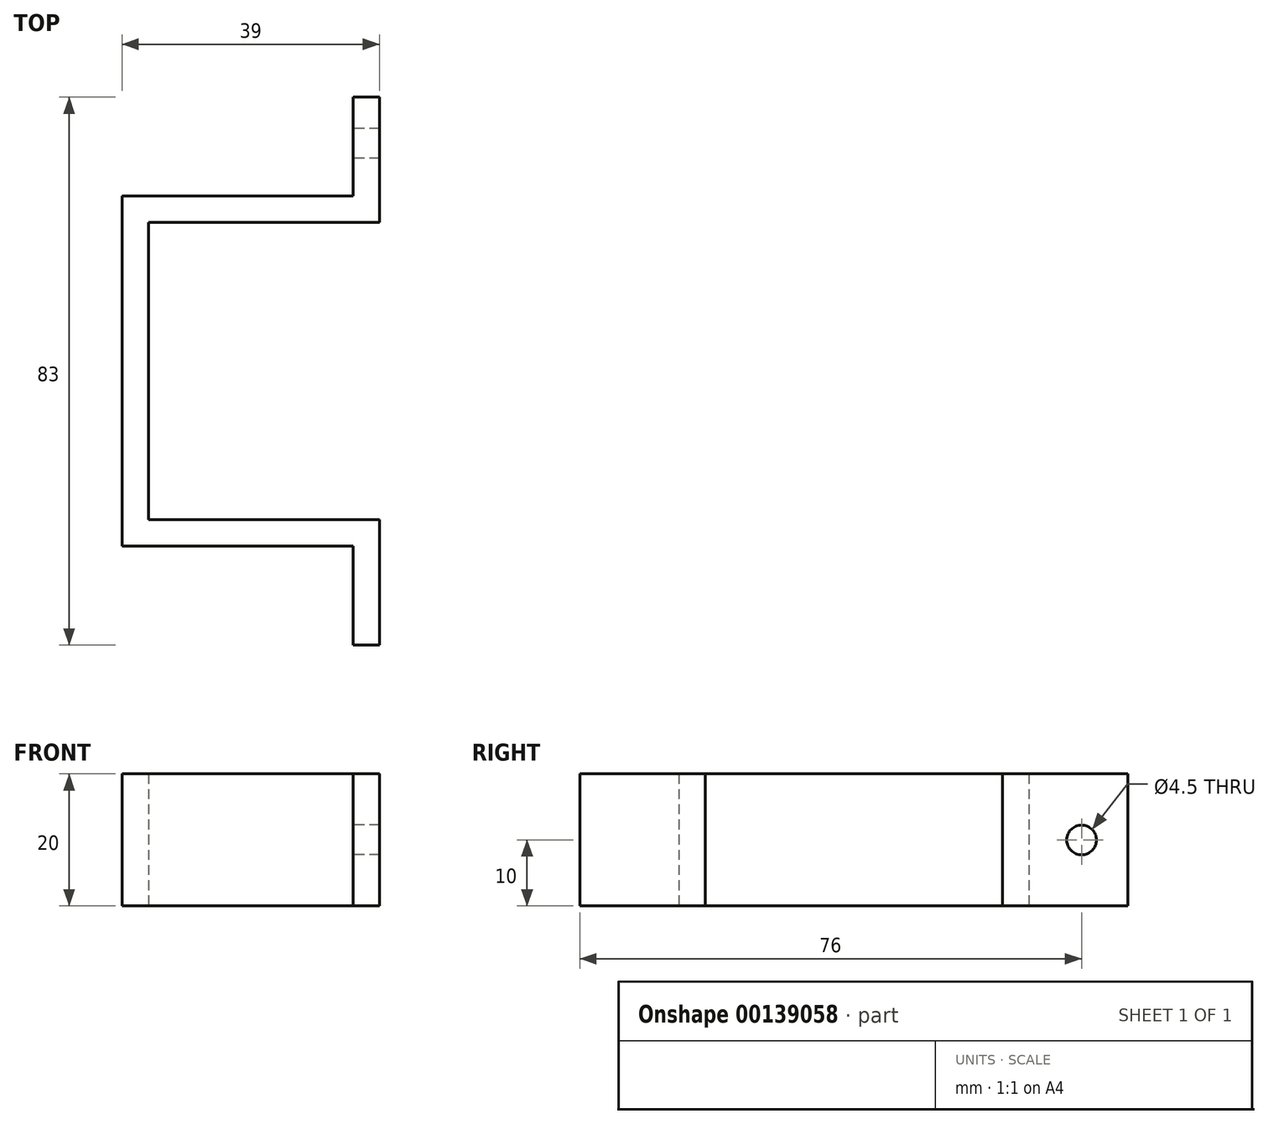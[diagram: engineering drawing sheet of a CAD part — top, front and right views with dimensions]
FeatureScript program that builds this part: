
annotation { "Feature Type Name" : "Feature", "Feature Type Description" : "" }
export const myFeature = defineFeature(function(context is Context, id is Id, definition is map)
    precondition{}
    {
        {
            var Q0;
            Q0=qCreatedBy(makeId("Top.planeOp"),FACE);
            var sketch = newSketch(context, id + "F0", { "sketchPlane" : qUnion([Q0])});
            skLineSegment(sketch, "E0", {"start": v(0, 0) * mm, "end": v(0, 26.5) * mm});
            skLineSegment(sketch, "E1", {"start": v(0, 26.5) * mm, "end": v(35, 26.5) * mm});
            skLineSegment(sketch, "E2", {"start": v(35, 26.5) * mm, "end": v(35, 41.5) * mm});
            skLineSegment(sketch, "E3", {"start": v(35, 41.5) * mm, "end": v(39, 41.5) * mm});
            skLineSegment(sketch, "E4", {"start": v(39, 41.5) * mm, "end": v(39, 22.5) * mm});
            skLineSegment(sketch, "E5", {"start": v(39, 22.5) * mm, "end": v(4, 22.5) * mm});
            skLineSegment(sketch, "E6", {"start": v(4, 22.5) * mm, "end": v(4, 0) * mm});
            skLineSegment(sketch, "E7", {"start": v(4, 0) * mm, "end": v(0, 0) * mm});
            skLineSegment(sketch, "E8.MirrorCS", {"start": v(35, -41.5) * mm, "end": v(39, -41.5) * mm});
            skLineSegment(sketch, "E9.MirrorCS", {"start": v(0, -26.5) * mm, "end": v(35, -26.5) * mm});
            skLineSegment(sketch, "E10.MirrorCS", {"start": v(0, 0) * mm, "end": v(0, -26.5) * mm});
            skLineSegment(sketch, "E11.MirrorCS", {"start": v(4, -22.5) * mm, "end": v(4, 0) * mm});
            skLineSegment(sketch, "E12.MirrorCS", {"start": v(35, -26.5) * mm, "end": v(35, -41.5) * mm});
            skLineSegment(sketch, "E13.MirrorCS", {"start": v(39, -41.5) * mm, "end": v(39, -22.5) * mm});
            skLineSegment(sketch, "E14.MirrorCS", {"start": v(39, -22.5) * mm, "end": v(4, -22.5) * mm});
            skSolve(sketch);
        }
        {
            var Q0;
            Q0=makeQuery(id+"F0.imprint","IMPRINT",FACE,{"disambiguationData":[TD([[makeQuery(id+"F0.imprint","IMPRINT",EDGE,{"derivedFrom":sQuery(id+"F0.wireOp",EDGE,"E0")}),-1.0]])]});
            var Q1;
            Q1=makeQuery(id+"F0.imprint","IMPRINT",FACE,{"disambiguationData":[TD([[makeQuery(id+"F0.imprint","IMPRINT",EDGE,{"derivedFrom":sQuery(id+"F0.wireOp",EDGE,"E7")}),1.0]])]});
            extrude(context, id + "F1", {"entities" : qUnion([Q0, Q1]), "depth" : 20 * mm});
        }
        {
            var Q0;
            Q0=qCreatedBy(makeId("Right.planeOp"),FACE);
            var sketch = newSketch(context, id + "F2", { "sketchPlane" : qUnion([Q0])});
            skCircle(sketch, "E15", {"center": v(34.5, 10) * mm, "radius": 2.25 * mm});
            skSolve(sketch);
        }
        {
            var Q0;
            Q0=makeQuery(id+"F2.imprint","IMPRINT",FACE,{"disambiguationData":[TD([[makeQuery(id+"F2.imprint","IMPRINT",EDGE,{"derivedFrom":sQuery(id+"F2.wireOp",EDGE,"E15")}),1.0]])]});
            extrude(context, id + "F3", {"entities" : qUnion([Q0]), "operationType" : NewBodyOperationType.REMOVE, "endBound" : BoundingType.THROUGH_ALL, "depth" : 25 * mm});
        }
    });
